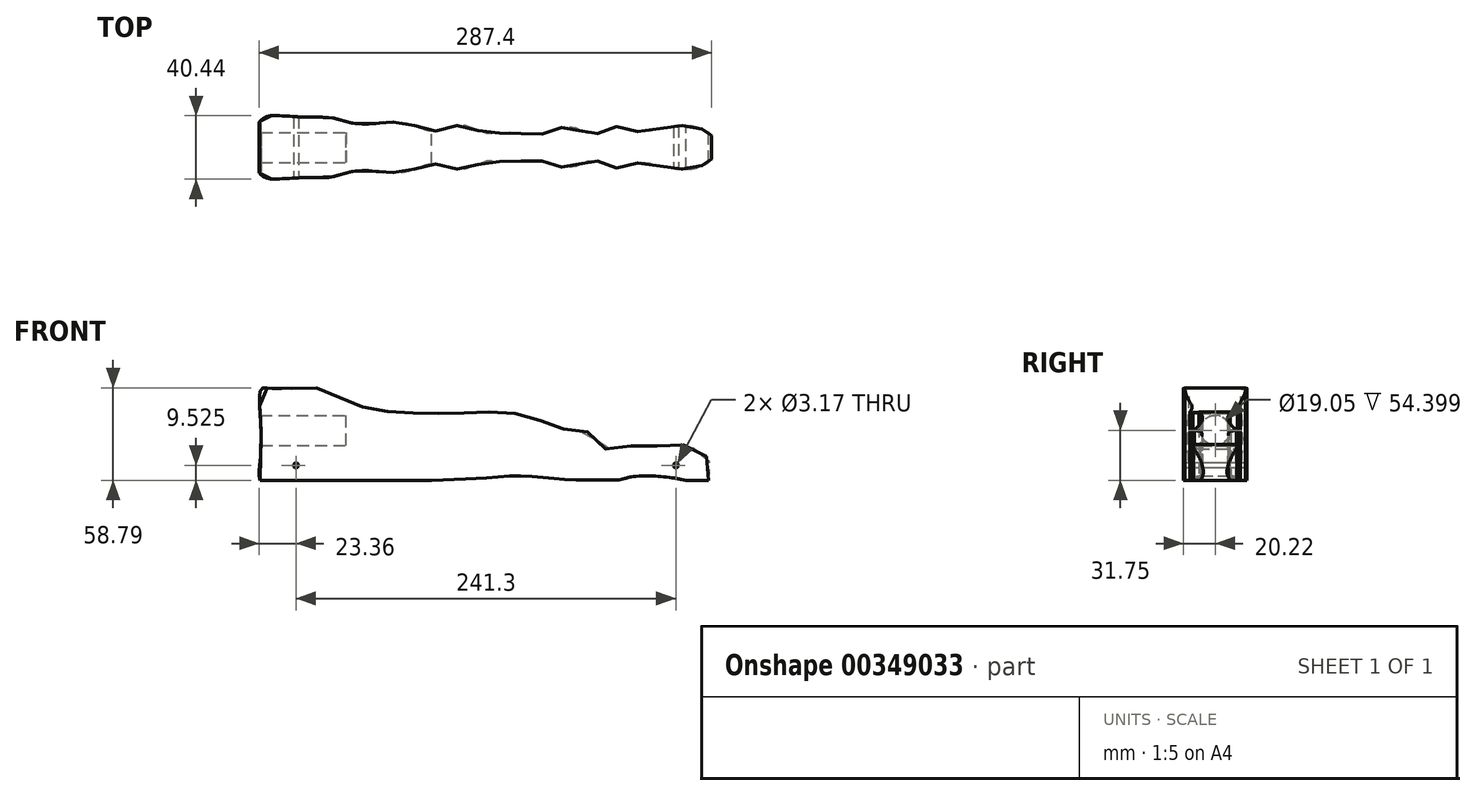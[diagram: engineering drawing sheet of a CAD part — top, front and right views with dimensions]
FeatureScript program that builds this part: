
annotation { "Feature Type Name" : "Feature", "Feature Type Description" : "" }
export const myFeature = defineFeature(function(context is Context, id is Id, definition is map)
    precondition{}
    {
        {
            var Q0;
            Q0=qCreatedBy(makeId("Front.planeOp"),FACE);
            var sketch = newSketch(context, id + "F0", { "sketchPlane" : qUnion([Q0])});
            skLineSegment(sketch, "E0.bottom", {"start": v(-146.05, 28.96) * mm, "end": v(146.05, 28.96) * mm, "construction": true});
            skLineSegment(sketch, "E0.top", {"start": v(-146.05, -34.54) * mm, "end": v(146.05, -34.54) * mm, "construction": true});
            skLineSegment(sketch, "E0.left", {"start": v(-146.05, 28.96) * mm, "end": v(-146.05, -34.54) * mm, "construction": true});
            skLineSegment(sketch, "E0.right", {"start": v(146.05, 28.96) * mm, "end": v(146.05, -34.54) * mm, "construction": true});
            skFitSpline(sketch, "E1", {"points": [v(-142.97, -32.6) * mm, v(-143.2, -16.67) * mm, v(-143.45, 12.1) * mm, v(-142.97, 26.1) * mm, v(-139.1, 26.9) * mm, v(-122.2, 26.58) * mm, v(-103.83, 26.1) * mm, v(-83, 16.18) * mm, v(-23.65, 10.82) * mm, v(18.35, 10.82) * mm, v(38.28, 4.6) * mm, v(53.5, 0) * mm, v(67, -2.25) * mm, v(72.87, -10.84) * mm, v(89.74, -10.24) * mm, v(112.2, -9.95) * mm, v(119.82, -8.9) * mm, v(127.69, -9.83) * mm, v(134.2, -12.46) * mm, v(141.66, -19.07) * mm, v(141.66, -31.42) * mm, v(119.95, -30.39) * mm, v(92.38, -29.57) * mm, v(84.5, -31.42) * mm, v(68.13, -31.42) * mm, v(55.49, -31.42) * mm, v(26, -29.09) * mm, v(10.54, -29.38) * mm, v(-15.65, -31.1) * mm, v(-51.66, -32.13) * mm, v(-70.02, -32.37) * mm, v(-91.76, -32.12) * mm, v(-106.25, -32.6) * mm, v(-122.2, -32.6) * mm, v(-136.69, -33.32) * mm, v(-142.97, -32.6) * mm]});
            skSolve(sketch);
        }
        {
            var Q0;
            Q0=qCreatedBy(makeId("Top.planeOp"),FACE);
            var sketch = newSketch(context, id + "F1", { "sketchPlane" : qUnion([Q0])});
            skLineSegment(sketch, "E2.bottom", {"start": v(-146.05, 22.22) * mm, "end": v(146.05, 22.23) * mm, "construction": true});
            skLineSegment(sketch, "E2.top", {"start": v(-146.05, -22.23) * mm, "end": v(146.05, -22.22) * mm, "construction": true});
            skLineSegment(sketch, "E2.left", {"start": v(-146.05, 22.22) * mm, "end": v(-146.05, -22.23) * mm, "construction": true});
            skLineSegment(sketch, "E2.right", {"start": v(146.05, 22.23) * mm, "end": v(146.05, -22.22) * mm, "construction": true});
            skLineSegment(sketch, "E3", {"start": v(-146.05, 0) * mm, "end": v(146.05, 0) * mm, "construction": true});
            skFitSpline(sketch, "E4", {"points": [v(-146.05, 0) * mm, v(-146.05, 12.35) * mm, v(-140.52, 18.98) * mm, v(-130.13, 20.1) * mm, v(-115.81, 19.26) * mm, v(-97.56, 18.7) * mm, v(-80.16, 14.77) * mm, v(-52.44, 15.72) * mm, v(-33.35, 10.39) * mm, v(-14.62, 14.14) * mm, v(0, 8.79) * mm, v(11.64, 9.44) * mm, v(29.85, 8.11) * mm, v(42.52, 10.56) * mm, v(53.75, 13.23) * mm, v(67.79, 8.31) * mm, v(83.97, 13.23) * mm, v(97.4, 9.69) * mm, v(108.78, 11.4) * mm, v(117.2, 13.3) * mm, v(127.59, 13.86) * mm, v(133.07, 13.2) * mm, v(142.61, 8.42) * mm, v(146.05, 0) * mm], "startDerivative": vector(-63.11, 321.29) * mm, "endDerivative": vector(51.94, -258) * mm});
            skFitSpline(sketch, "E5.MirrorCS", {"points": [v(-146.05, 0) * mm, v(-146.05, -12.35) * mm, v(-140.52, -18.98) * mm, v(-130.13, -20.1) * mm, v(-115.81, -19.26) * mm, v(-97.56, -18.7) * mm, v(-80.16, -14.77) * mm, v(-52.44, -15.72) * mm, v(-33.35, -10.39) * mm, v(-14.62, -14.14) * mm, v(0, -8.79) * mm, v(11.64, -9.44) * mm, v(29.85, -8.11) * mm, v(42.52, -10.56) * mm, v(53.75, -13.23) * mm, v(67.79, -8.31) * mm, v(83.97, -13.23) * mm, v(97.4, -9.69) * mm, v(108.78, -11.4) * mm, v(117.2, -13.3) * mm, v(127.59, -13.86) * mm, v(133.07, -13.2) * mm, v(142.61, -8.42) * mm, v(146.05, 0) * mm], "startDerivative": vector(-63.11, -321.29) * mm, "endDerivative": vector(51.94, 258) * mm});
            skLineSegment(sketch, "E6.MirrorCS", {"start": v(-146.05, -22.23) * mm, "end": v(146.05, -22.22) * mm});
            skSolve(sketch);
        }
        {
            var Q0;
            Q0=qCreatedBy(makeId("Right.planeOp"),FACE);
            var sketch = newSketch(context, id + "F2", { "sketchPlane" : qUnion([Q0])});
            skCircle(sketch, "E7", {"center": v(0, 0) * mm, "radius": 9.53 * mm});
            skSolve(sketch);
        }
        {
            var Q0;
            Q0=qCreatedBy(makeId("Front.planeOp"),FACE);
            var sketch = newSketch(context, id + "F3", { "sketchPlane" : qUnion([Q0])});
            skCircle(sketch, "E8", {"center": v(-120.65, -22.22) * mm, "radius": 1.59 * mm});
            skCircle(sketch, "E9", {"center": v(120.65, -22.23) * mm, "radius": 1.59 * mm});
            skSolve(sketch);
        }
        {
            var Q0;
            Q0=qSketchRegion(id+"F0",true);
            extrude(context, id + "F4", {"entities" : qUnion([Q0]), "depth" : 44.45 * mm, "symmetric" : true});
        }
        {
            var Q0;
            Q0=makeQuery(id+"F1.imprint","IMPRINT",FACE,{"disambiguationData":[TD([[makeQuery(id+"F1.imprint","IMPRINT",EDGE,{"derivedFrom":sQuery(id+"F1.wireOp",EDGE,"E4")}),-1.0]])]});
            var Q1;
            Q1=sQuery(id+"F1.wireOp",EDGE,"E5.MirrorCS");
            var Q2;
            Q2=sQuery(id+"F1.wireOp",EDGE,"E4");
            extrude(context, id + "F5", {"entities" : qUnion([Q0]), "operationType" : NewBodyOperationType.INTERSECT, "surfaceEntities" : qUnion([Q1, Q2]), "oppositeDirection" : true, "depth" : 63.5 * mm, "symmetric" : true});
        }
        {
            var Q0;
            Q0=qSketchRegion(id+"F2",true);
            extrude(context, id + "F6", {"entities" : qUnion([Q0]), "operationType" : NewBodyOperationType.REMOVE, "oppositeDirection" : true, "depth" : 152.4 * mm, "hasSecondDirection" : true, "secondDirectionOppositeDirection" : true, "secondDirectionDepth" : 88.9 * mm});
        }
        {
            var Q0;
            Q0=qSketchRegion(id+"F3",true);
            extrude(context, id + "F7", {"entities" : qUnion([Q0]), "operationType" : NewBodyOperationType.REMOVE, "oppositeDirection" : true, "depth" : 50.8 * mm, "symmetric" : true});
        }
    });
